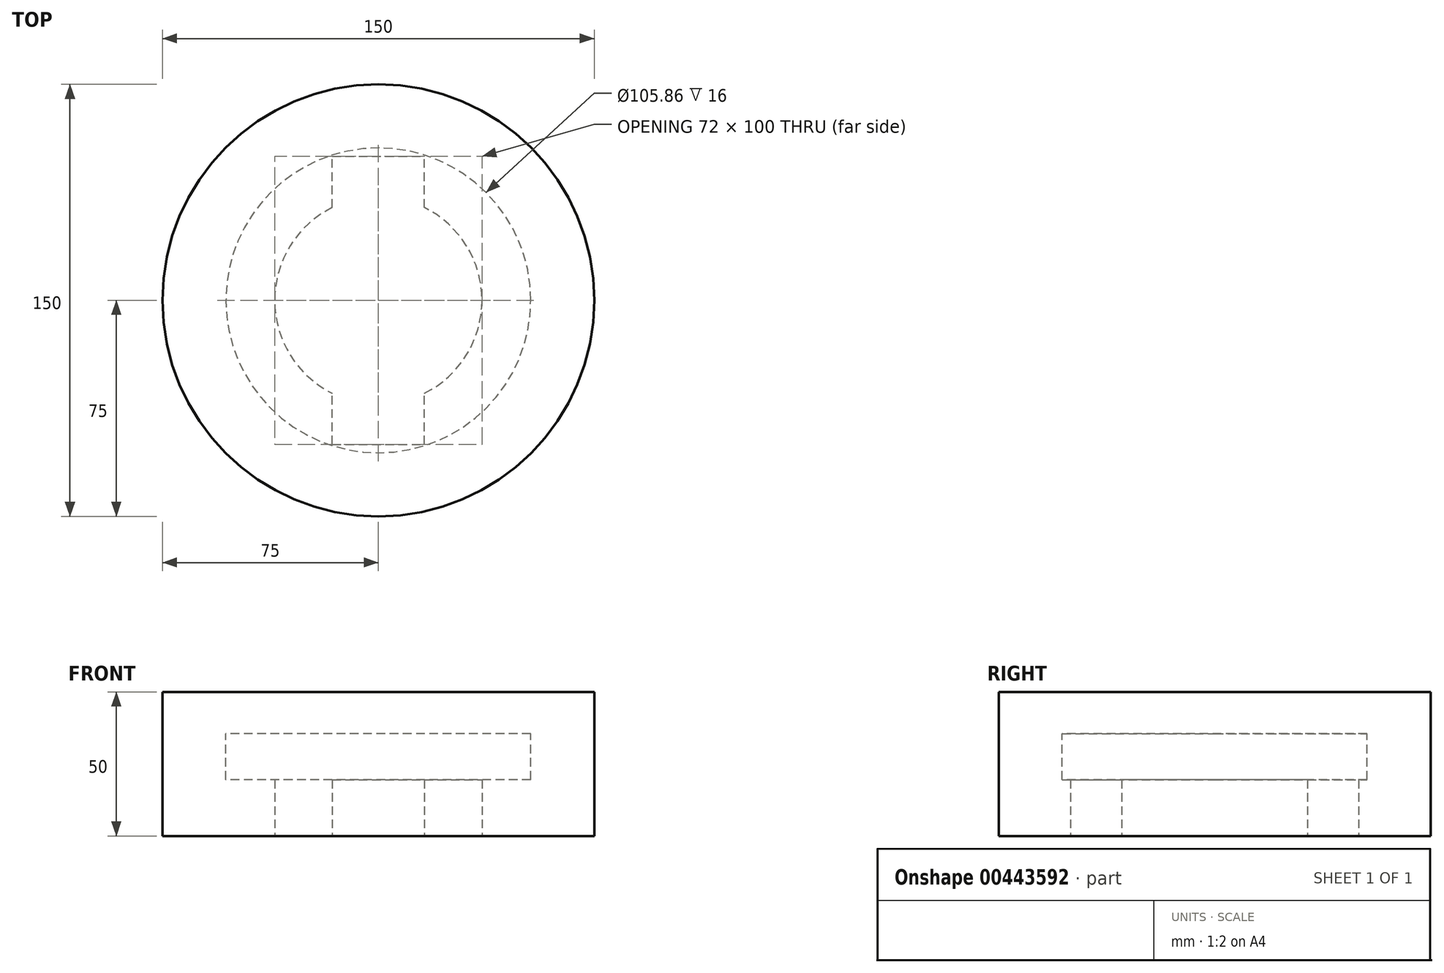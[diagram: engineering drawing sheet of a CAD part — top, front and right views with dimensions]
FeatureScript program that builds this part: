
annotation { "Feature Type Name" : "Feature", "Feature Type Description" : "" }
export const myFeature = defineFeature(function(context is Context, id is Id, definition is map)
    precondition{}
    {
        {
            var Q0;
            Q0=qCreatedBy(makeId("Top.planeOp"),FACE);
            var sketch = newSketch(context, id + "F0", { "sketchPlane" : qUnion([Q0])});
            skCircle(sketch, "E0", {"center": v(0, 0) * mm, "radius": 75 * mm});
            skSolve(sketch);
        }
        {
            var Q0;
            Q0 = qSketchRegion(id + "F0", true);
            extrude(context, id + "F1", {"entities" : qUnion([Q0]), "depth" : 50 * mm});
        }
        {
            var Q0;
            Q0=makeQuery(id+"F1.opExtrude","CAP_FACE",FACE,{"disambiguationData":[OSD([sQuery(id+"F0.wireOp",EDGE,"E0")])],"isStart":true});
            var sketch = newSketch(context, id + "F2", { "sketchPlane" : qUnion([Q0])});
            skCircle(sketch, "E1", {"center": v(0, 0) * mm, "radius": 36 * mm});
            skLineSegment(sketch, "E2.bottom", {"start": v(-16, 50) * mm, "end": v(16, 50) * mm});
            skLineSegment(sketch, "E2.top", {"start": v(-16, 28.5) * mm, "end": v(16, 28.5) * mm});
            skLineSegment(sketch, "E2.left", {"start": v(-16, 50) * mm, "end": v(-16, 28.5) * mm});
            skLineSegment(sketch, "E2.right", {"start": v(16, 50) * mm, "end": v(16, 28.5) * mm});
            skLineSegment(sketch, "E3.bottom", {"start": v(-16, -28.5) * mm, "end": v(16, -28.5) * mm});
            skLineSegment(sketch, "E3.top", {"start": v(-16, -50) * mm, "end": v(16, -50) * mm});
            skLineSegment(sketch, "E3.left", {"start": v(-16, -28.5) * mm, "end": v(-16, -50) * mm});
            skLineSegment(sketch, "E3.right", {"start": v(16, -28.5) * mm, "end": v(16, -50) * mm});
            skSolve(sketch);
        }
        {
            var Q0;
            Q0 = qSketchRegion(id + "F2", true);
            extrude(context, id + "F3", {"entities" : qUnion([Q0]), "operationType" : NewBodyOperationType.REMOVE, "oppositeDirection" : true, "depth" : 35.5 * mm});
        }
        {
            var Q0;
            Q0=qCreatedBy(makeId("Top.planeOp"),FACE);
            cPlane(context, id + "F4", {"entities" : qUnion([Q0]), "cplaneType" : CPlaneType.OFFSET, "offset" : 35.5 * mm, "width" : 150 * mm, "height" : 150 * mm});
        }
        {
            var Q0;
            Q0=qCreatedBy(id+"F4.planeOp",FACE);
            var sketch = newSketch(context, id + "F5", { "sketchPlane" : qUnion([Q0])});
            skCircle(sketch, "E4", {"center": v(0, 0) * mm, "radius": 52.93 * mm});
            skSolve(sketch);
        }
        {
            var Q0;
            Q0 = qSketchRegion(id + "F5", true);
            extrude(context, id + "F6", {"entities" : qUnion([Q0]), "operationType" : NewBodyOperationType.REMOVE, "oppositeDirection" : true, "depth" : 16 * mm});
        }
    });
